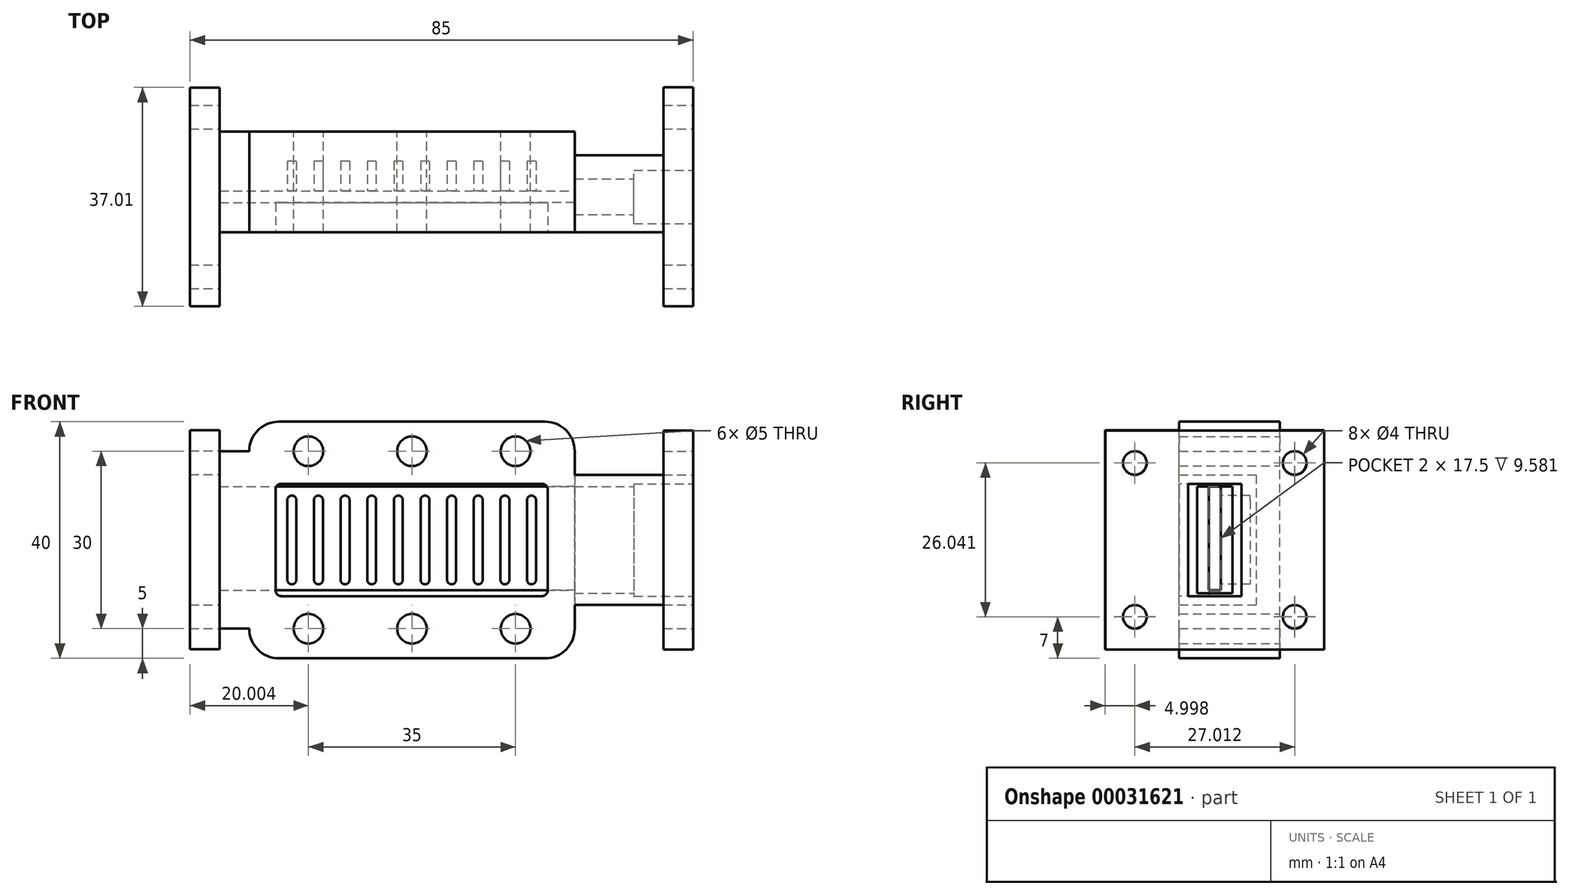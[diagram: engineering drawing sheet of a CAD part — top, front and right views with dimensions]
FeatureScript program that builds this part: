
annotation { "Feature Type Name" : "Feature", "Feature Type Description" : "" }
export const myFeature = defineFeature(function(context is Context, id is Id, definition is map)
    precondition{}
    {
        {
            var Q0;
            Q0=qCreatedBy(makeId("Front.planeOp"),FACE);
            var sketch = newSketch(context, id + "F0", { "sketchPlane" : qUnion([Q0])});
            skLineSegment(sketch, "E0.bottom", {"start": v(22.55, -20) * mm, "end": v(-22.45, -20) * mm});
            skLineSegment(sketch, "E0.top", {"start": v(22.55, 20) * mm, "end": v(-22.45, 20) * mm});
            skLineSegment(sketch, "E0.left", {"start": v(27.55, -15) * mm, "end": v(27.55, 15) * mm});
            skLineSegment(sketch, "E0.right", {"start": v(-27.45, -15) * mm, "end": v(-27.45, 15) * mm});
            skCircle(sketch, "E1", {"center": v(-17.45, 15) * mm, "radius": 2.5 * mm});
            skLineSegment(sketch, "E2", {"start": v(-40.3, 0) * mm, "end": v(38.37, 0) * mm, "construction": true});
            skCircle(sketch, "E3.MirrorC", {"center": v(-17.45, -15) * mm, "radius": 2.5 * mm});
            skCircle(sketch, "E4", {"center": v(0.05, 15) * mm, "radius": 2.5 * mm});
            skCircle(sketch, "E5", {"center": v(17.55, 15) * mm, "radius": 2.5 * mm});
            skCircle(sketch, "E6.MirrorC", {"center": v(0.05, -15) * mm, "radius": 2.5 * mm});
            skCircle(sketch, "E7.MirrorC", {"center": v(17.55, -15) * mm, "radius": 2.5 * mm});
            skPoint(sketch, "E8.visualSharp", {"position": v(-27.45, 20) * mm});
            skArc(sketch, "E8.filletArc", {"start": v(-22.45, 20) * mm, "mid": v(-25.98, 18.54) * mm, "end": v(-27.45, 15) * mm});
            skPoint(sketch, "E9.visualSharp", {"position": v(-27.45, -20) * mm});
            skArc(sketch, "E9.filletArc", {"start": v(-27.45, -15) * mm, "mid": v(-25.98, -18.54) * mm, "end": v(-22.45, -20) * mm});
            skPoint(sketch, "E10.visualSharp", {"position": v(27.55, -20) * mm});
            skArc(sketch, "E10.filletArc", {"start": v(22.55, -20) * mm, "mid": v(26.09, -18.54) * mm, "end": v(27.55, -15) * mm});
            skPoint(sketch, "E11.visualSharp", {"position": v(27.55, 20) * mm});
            skArc(sketch, "E11.filletArc", {"start": v(27.55, 15) * mm, "mid": v(26.09, 18.54) * mm, "end": v(22.55, 20) * mm});
            skSolve(sketch);
        }
        {
            var Q0;
            Q0=makeQuery(id+"F0.imprint","IMPRINT",FACE,{"disambiguationData":[TD([[makeQuery(id+"F0.imprint","IMPRINT",EDGE,{"derivedFrom":sQuery(id+"F0.wireOp",EDGE,"E0.bottom")}),-1.0]])]});
            extrude(context, id + "F1", {"entities" : qUnion([Q0]), "depth" : 17 * mm});
        }
        {
            var Q0;
            Q0=makeQuery(id+"F1.opExtrude","CAP_FACE",FACE,{"disambiguationData":[OSD([sQuery(id+"F0.wireOp",EDGE,"E0.bottom"),sQuery(id+"F0.wireOp",EDGE,"E0.top"),sQuery(id+"F0.wireOp",EDGE,"E0.left"),sQuery(id+"F0.wireOp",EDGE,"E0.right"),sQuery(id+"F0.wireOp",EDGE,"E1"),sQuery(id+"F0.wireOp",EDGE,"E3.MirrorC"),sQuery(id+"F0.wireOp",EDGE,"E4"),sQuery(id+"F0.wireOp",EDGE,"E5"),sQuery(id+"F0.wireOp",EDGE,"E6.MirrorC"),sQuery(id+"F0.wireOp",EDGE,"E7.MirrorC"),sQuery(id+"F0.wireOp",EDGE,"E8.filletArc"),sQuery(id+"F0.wireOp",EDGE,"E9.filletArc"),sQuery(id+"F0.wireOp",EDGE,"E10.filletArc"),sQuery(id+"F0.wireOp",EDGE,"E11.filletArc")])],"isStart":false});
            var sketch = newSketch(context, id + "F2", { "sketchPlane" : qUnion([Q0])});
            skLineSegment(sketch, "E12.bottom", {"start": v(-22, 9.5) * mm, "end": v(22, 9.5) * mm});
            skLineSegment(sketch, "E12.top", {"start": v(-22, -9.5) * mm, "end": v(22, -9.5) * mm});
            skLineSegment(sketch, "E12.left", {"start": v(-23, 8.5) * mm, "end": v(-23, -8.5) * mm});
            skLineSegment(sketch, "E12.right", {"start": v(23, 8.5) * mm, "end": v(23, -8.5) * mm});
            skLineSegment(sketch, "E13", {"start": v(-42.5, 0) * mm, "end": v(36.74, 0) * mm, "construction": true});
            skLineSegment(sketch, "E14", {"start": v(0, 24.37) * mm, "end": v(0, -28.4) * mm, "construction": true});
            skPoint(sketch, "E15.visualSharp", {"position": v(-23, 9.5) * mm});
            skArc(sketch, "E15.filletArc", {"start": v(-22, 9.5) * mm, "mid": v(-22.7, 9.2) * mm, "end": v(-23, 8.5) * mm});
            skPoint(sketch, "E16.visualSharp", {"position": v(-23, -9.5) * mm});
            skArc(sketch, "E16.filletArc", {"start": v(-23, -8.5) * mm, "mid": v(-22.7, -9.2) * mm, "end": v(-22, -9.5) * mm});
            skPoint(sketch, "E17.visualSharp", {"position": v(23, -9.5) * mm});
            skArc(sketch, "E17.filletArc", {"start": v(22, -9.5) * mm, "mid": v(22.7, -9.2) * mm, "end": v(23, -8.5) * mm});
            skPoint(sketch, "E18.visualSharp", {"position": v(23, 9.5) * mm});
            skArc(sketch, "E18.filletArc", {"start": v(23, 8.5) * mm, "mid": v(22.7, 9.2) * mm, "end": v(22, 9.5) * mm});
            skSolve(sketch);
        }
        {
            var Q0;
            Q0 = qSketchRegion(id + "F2", true);
            extrude(context, id + "F3", {"entities" : qUnion([Q0]), "operationType" : NewBodyOperationType.REMOVE, "oppositeDirection" : true, "depth" : 5 * mm});
        }
        {
            var Q0;
            Q0=makeQuery(id+"F3.boolean.opBoolean","COPY",FACE,{"derivedFrom":makeQuery(id+"F3.opExtrude","CAP_FACE",FACE,{"disambiguationData":[OSD([sQuery(id+"F2.wireOp",EDGE,"E12.bottom"),sQuery(id+"F2.wireOp",EDGE,"E12.top"),sQuery(id+"F2.wireOp",EDGE,"E12.left"),sQuery(id+"F2.wireOp",EDGE,"E12.right"),sQuery(id+"F2.wireOp",EDGE,"E15.filletArc"),sQuery(id+"F2.wireOp",EDGE,"E16.filletArc"),sQuery(id+"F2.wireOp",EDGE,"E17.filletArc"),sQuery(id+"F2.wireOp",EDGE,"E18.filletArc")])],"isStart":false})});
            var sketch = newSketch(context, id + "F4", { "sketchPlane" : qUnion([Q0])});
            skLineSegment(sketch, "E19.bottom", {"start": v(-23, 8.5) * mm, "end": v(23, 8.5) * mm});
            skLineSegment(sketch, "E19.top", {"start": v(-23, -8.5) * mm, "end": v(23, -8.5) * mm});
            skLineSegment(sketch, "E19.left", {"start": v(-23, 8.5) * mm, "end": v(-23, -8.5) * mm});
            skLineSegment(sketch, "E20", {"start": v(0, 22.62) * mm, "end": v(0, -29.48) * mm, "construction": true});
            skLineSegment(sketch, "E21", {"start": v(23, 8.5) * mm, "end": v(23, -8.5) * mm});
            skSolve(sketch);
        }
        {
            var Q0;
            Q0 = qSketchRegion(id + "F4", true);
            extrude(context, id + "F5", {"entities" : qUnion([Q0]), "operationType" : NewBodyOperationType.REMOVE, "oppositeDirection" : true, "depth" : 2 * mm});
        }
        {
            var Q0;
            Q0=makeQuery(id+"F5.boolean.opBoolean","COPY",FACE,{"derivedFrom":makeQuery(id+"F5.opExtrude","CAP_FACE",FACE,{"disambiguationData":[OSD([sQuery(id+"F4.wireOp",EDGE,"E19.bottom"),sQuery(id+"F4.wireOp",EDGE,"E19.top"),sQuery(id+"F4.wireOp",EDGE,"E19.left"),sQuery(id+"F4.wireOp",EDGE,"E21")])],"isStart":false})});
            var sketch = newSketch(context, id + "F6", { "sketchPlane" : qUnion([Q0])});
            skLineSegment(sketch, "E22.bottom", {"start": v(-20.25, 7.5) * mm, "end": v(-20.25, 7.5) * mm});
            skLineSegment(sketch, "E22.top", {"start": v(-20.25, -7.5) * mm, "end": v(-20.25, -7.5) * mm});
            skLineSegment(sketch, "E22.left", {"start": v(-21, 6.75) * mm, "end": v(-21, -6.75) * mm});
            skLineSegment(sketch, "E22.right", {"start": v(-19.5, 6.75) * mm, "end": v(-19.5, -6.75) * mm});
            skPoint(sketch, "E23.visualSharp", {"position": v(22.5, 9) * mm});
            skPoint(sketch, "E24.visualSharp", {"position": v(22.5, -9) * mm});
            skPoint(sketch, "E25.visualSharp", {"position": v(-22.5, -9) * mm});
            skPoint(sketch, "E26.visualSharp", {"position": v(-19.5, 7.5) * mm});
            skArc(sketch, "E26.filletArc", {"start": v(-19.5, 6.75) * mm, "mid": v(-19.72, 7.28) * mm, "end": v(-20.25, 7.5) * mm});
            skPoint(sketch, "E27.visualSharp", {"position": v(-21, 7.5) * mm});
            skArc(sketch, "E27.filletArc", {"start": v(-20.25, 7.5) * mm, "mid": v(-20.78, 7.28) * mm, "end": v(-21, 6.75) * mm});
            skPoint(sketch, "E28.visualSharp", {"position": v(-21, -7.5) * mm});
            skArc(sketch, "E28.filletArc", {"start": v(-21, -6.75) * mm, "mid": v(-20.78, -7.28) * mm, "end": v(-20.25, -7.5) * mm});
            skPoint(sketch, "E29.visualSharp", {"position": v(-19.5, -7.5) * mm});
            skArc(sketch, "E29.filletArc", {"start": v(-20.25, -7.5) * mm, "mid": v(-19.72, -7.28) * mm, "end": v(-19.5, -6.75) * mm});
            skLineSegment(sketch, "E30.1.0.0", {"start": v(-16.5, 6.75) * mm, "end": v(-16.5, -6.75) * mm});
            skArc(sketch, "E30.1.0.1", {"start": v(-15.75, 7.5) * mm, "mid": v(-16.28, 7.28) * mm, "end": v(-16.5, 6.75) * mm});
            skArc(sketch, "E30.1.0.2", {"start": v(-15, 6.75) * mm, "mid": v(-15.22, 7.28) * mm, "end": v(-15.75, 7.5) * mm});
            skLineSegment(sketch, "E30.1.0.3", {"start": v(-15, 6.75) * mm, "end": v(-15, -6.75) * mm});
            skArc(sketch, "E30.1.0.4", {"start": v(-15.75, -7.5) * mm, "mid": v(-15.22, -7.28) * mm, "end": v(-15, -6.75) * mm});
            skArc(sketch, "E30.1.0.5", {"start": v(-16.5, -6.75) * mm, "mid": v(-16.28, -7.28) * mm, "end": v(-15.75, -7.5) * mm});
            skLineSegment(sketch, "E30.2.0.0", {"start": v(-12, 6.75) * mm, "end": v(-12, -6.75) * mm});
            skArc(sketch, "E30.2.0.1", {"start": v(-11.25, 7.5) * mm, "mid": v(-11.78, 7.28) * mm, "end": v(-12, 6.75) * mm});
            skArc(sketch, "E30.2.0.2", {"start": v(-10.5, 6.75) * mm, "mid": v(-10.72, 7.28) * mm, "end": v(-11.25, 7.5) * mm});
            skLineSegment(sketch, "E30.2.0.3", {"start": v(-10.5, 6.75) * mm, "end": v(-10.5, -6.75) * mm});
            skArc(sketch, "E30.2.0.4", {"start": v(-11.25, -7.5) * mm, "mid": v(-10.72, -7.28) * mm, "end": v(-10.5, -6.75) * mm});
            skArc(sketch, "E30.2.0.5", {"start": v(-12, -6.75) * mm, "mid": v(-11.78, -7.28) * mm, "end": v(-11.25, -7.5) * mm});
            skLineSegment(sketch, "E30.direction1", {"start": v(-21, -6.75) * mm, "end": v(-16.5, -6.75) * mm, "construction": true});
            skLineSegment(sketch, "E31.0.3.0", {"start": v(-7.5, 6.75) * mm, "end": v(-7.5, -6.75) * mm});
            skArc(sketch, "E31.3.3.0", {"start": v(-6.75, 7.5) * mm, "mid": v(-7.28, 7.28) * mm, "end": v(-7.5, 6.75) * mm});
            skArc(sketch, "E31.7.3.0", {"start": v(-6, 6.75) * mm, "mid": v(-6.22, 7.28) * mm, "end": v(-6.75, 7.5) * mm});
            skLineSegment(sketch, "E31.11.3.0", {"start": v(-6, 6.75) * mm, "end": v(-6, -6.75) * mm});
            skArc(sketch, "E31.14.3.0", {"start": v(-6.75, -7.5) * mm, "mid": v(-6.22, -7.28) * mm, "end": v(-6, -6.75) * mm});
            skArc(sketch, "E31.18.3.0", {"start": v(-7.5, -6.75) * mm, "mid": v(-7.28, -7.28) * mm, "end": v(-6.75, -7.5) * mm});
            skLineSegment(sketch, "E31.0.4.0", {"start": v(-3, 6.75) * mm, "end": v(-3, -6.75) * mm});
            skArc(sketch, "E31.3.4.0", {"start": v(-2.25, 7.5) * mm, "mid": v(-2.78, 7.28) * mm, "end": v(-3, 6.75) * mm});
            skArc(sketch, "E31.7.4.0", {"start": v(-1.5, 6.75) * mm, "mid": v(-1.72, 7.28) * mm, "end": v(-2.25, 7.5) * mm});
            skLineSegment(sketch, "E31.11.4.0", {"start": v(-1.5, 6.75) * mm, "end": v(-1.5, -6.75) * mm});
            skArc(sketch, "E31.14.4.0", {"start": v(-2.25, -7.5) * mm, "mid": v(-1.72, -7.28) * mm, "end": v(-1.5, -6.75) * mm});
            skArc(sketch, "E31.18.4.0", {"start": v(-3, -6.75) * mm, "mid": v(-2.78, -7.28) * mm, "end": v(-2.25, -7.5) * mm});
            skLineSegment(sketch, "E31.0.5.0", {"start": v(1.5, 6.75) * mm, "end": v(1.5, -6.75) * mm});
            skArc(sketch, "E31.3.5.0", {"start": v(2.25, 7.5) * mm, "mid": v(1.72, 7.28) * mm, "end": v(1.5, 6.75) * mm});
            skArc(sketch, "E31.7.5.0", {"start": v(3, 6.75) * mm, "mid": v(2.78, 7.28) * mm, "end": v(2.25, 7.5) * mm});
            skLineSegment(sketch, "E31.11.5.0", {"start": v(3, 6.75) * mm, "end": v(3, -6.75) * mm});
            skArc(sketch, "E31.14.5.0", {"start": v(2.25, -7.5) * mm, "mid": v(2.78, -7.28) * mm, "end": v(3, -6.75) * mm});
            skArc(sketch, "E31.18.5.0", {"start": v(1.5, -6.75) * mm, "mid": v(1.72, -7.28) * mm, "end": v(2.25, -7.5) * mm});
            skLineSegment(sketch, "E31.0.6.0", {"start": v(6, 6.75) * mm, "end": v(6, -6.75) * mm});
            skArc(sketch, "E31.3.6.0", {"start": v(6.75, 7.5) * mm, "mid": v(6.22, 7.28) * mm, "end": v(6, 6.75) * mm});
            skArc(sketch, "E31.7.6.0", {"start": v(7.5, 6.75) * mm, "mid": v(7.28, 7.28) * mm, "end": v(6.75, 7.5) * mm});
            skLineSegment(sketch, "E31.11.6.0", {"start": v(7.5, 6.75) * mm, "end": v(7.5, -6.75) * mm});
            skArc(sketch, "E31.14.6.0", {"start": v(6.75, -7.5) * mm, "mid": v(7.28, -7.28) * mm, "end": v(7.5, -6.75) * mm});
            skArc(sketch, "E31.18.6.0", {"start": v(6, -6.75) * mm, "mid": v(6.22, -7.28) * mm, "end": v(6.75, -7.5) * mm});
            skLineSegment(sketch, "E31.0.7.0", {"start": v(10.5, 6.75) * mm, "end": v(10.5, -6.75) * mm});
            skArc(sketch, "E31.3.7.0", {"start": v(11.25, 7.5) * mm, "mid": v(10.72, 7.28) * mm, "end": v(10.5, 6.75) * mm});
            skArc(sketch, "E31.7.7.0", {"start": v(12, 6.75) * mm, "mid": v(11.78, 7.28) * mm, "end": v(11.25, 7.5) * mm});
            skLineSegment(sketch, "E31.11.7.0", {"start": v(12, 6.75) * mm, "end": v(12, -6.75) * mm});
            skArc(sketch, "E31.14.7.0", {"start": v(11.25, -7.5) * mm, "mid": v(11.78, -7.28) * mm, "end": v(12, -6.75) * mm});
            skArc(sketch, "E31.18.7.0", {"start": v(10.5, -6.75) * mm, "mid": v(10.72, -7.28) * mm, "end": v(11.25, -7.5) * mm});
            skLineSegment(sketch, "E31.0.8.0", {"start": v(15, 6.75) * mm, "end": v(15, -6.75) * mm});
            skArc(sketch, "E31.3.8.0", {"start": v(15.75, 7.5) * mm, "mid": v(15.22, 7.28) * mm, "end": v(15, 6.75) * mm});
            skArc(sketch, "E31.7.8.0", {"start": v(16.5, 6.75) * mm, "mid": v(16.28, 7.28) * mm, "end": v(15.75, 7.5) * mm});
            skLineSegment(sketch, "E31.11.8.0", {"start": v(16.5, 6.75) * mm, "end": v(16.5, -6.75) * mm});
            skArc(sketch, "E31.14.8.0", {"start": v(15.75, -7.5) * mm, "mid": v(16.28, -7.28) * mm, "end": v(16.5, -6.75) * mm});
            skArc(sketch, "E31.18.8.0", {"start": v(15, -6.75) * mm, "mid": v(15.22, -7.28) * mm, "end": v(15.75, -7.5) * mm});
            skLineSegment(sketch, "E31.0.9.0", {"start": v(19.5, 6.75) * mm, "end": v(19.5, -6.75) * mm});
            skArc(sketch, "E31.3.9.0", {"start": v(20.25, 7.5) * mm, "mid": v(19.72, 7.28) * mm, "end": v(19.5, 6.75) * mm});
            skArc(sketch, "E31.7.9.0", {"start": v(21, 6.75) * mm, "mid": v(20.78, 7.28) * mm, "end": v(20.25, 7.5) * mm});
            skLineSegment(sketch, "E31.11.9.0", {"start": v(21, 6.75) * mm, "end": v(21, -6.75) * mm});
            skArc(sketch, "E31.14.9.0", {"start": v(20.25, -7.5) * mm, "mid": v(20.78, -7.28) * mm, "end": v(21, -6.75) * mm});
            skArc(sketch, "E31.18.9.0", {"start": v(19.5, -6.75) * mm, "mid": v(19.72, -7.28) * mm, "end": v(20.25, -7.5) * mm});
            skSolve(sketch);
        }
        {
            var Q0;
            Q0 = qSketchRegion(id + "F6", true);
            extrude(context, id + "F7", {"entities" : qUnion([Q0]), "operationType" : NewBodyOperationType.REMOVE, "oppositeDirection" : true, "depth" : 5 * mm});
        }
        {
            var Q0;
            Q0=makeQuery(id+"F1.opExtrude","SWEPT_FACE",FACE,{"disambiguationData":[OSD([sQuery(id+"F0.wireOp",EDGE,"E0.right")])]});
            var sketch = newSketch(context, id + "F8", { "sketchPlane" : qUnion([Q0])});
            skLineSegment(sketch, "E32.bottom", {"start": v(10, 9) * mm, "end": v(12, 9) * mm});
            skLineSegment(sketch, "E32.top", {"start": v(10, -8.5) * mm, "end": v(12, -8.5) * mm});
            skLineSegment(sketch, "E32.left", {"start": v(10, 9) * mm, "end": v(10, -8.5) * mm});
            skLineSegment(sketch, "E32.right", {"start": v(12, 9) * mm, "end": v(12, -8.5) * mm});
            skLineSegment(sketch, "E33", {"start": v(23.3, 0) * mm, "end": v(0, 0) * mm, "construction": true});
            skSolve(sketch);
        }
        {
            var Q0;
            Q0=makeQuery(id+"F1.opExtrude","SWEPT_FACE",FACE,{"disambiguationData":[OSD([sQuery(id+"F0.wireOp",EDGE,"E0.left")])]});
            var sketch = newSketch(context, id + "F9", { "sketchPlane" : qUnion([Q0])});
            skLineSegment(sketch, "E34.bottom", {"start": v(-17, 11) * mm, "end": v(-4, 11) * mm});
            skLineSegment(sketch, "E34.top", {"start": v(-17, -11) * mm, "end": v(-4, -11) * mm});
            skLineSegment(sketch, "E34.left", {"start": v(-17, 11) * mm, "end": v(-17, -11) * mm});
            skLineSegment(sketch, "E34.right", {"start": v(-4, 11) * mm, "end": v(-4, -11) * mm});
            skLineSegment(sketch, "E35", {"start": v(-20.32, 0) * mm, "end": v(5.52, 0) * mm, "construction": true});
            skLineSegment(sketch, "E36", {"start": v(0, 0) * mm, "end": v(0, 23.79) * mm, "construction": true});
            skSolve(sketch);
        }
        {
            var Q0;
            Q0 = qSketchRegion(id + "F9", true);
            extrude(context, id + "F10", {"entities" : qUnion([Q0]), "operationType" : NewBodyOperationType.ADD, "depth" : 20 * mm});
        }
        {
            var Q0;
            Q0=makeQuery(id+"F10.opExtrude","CAP_FACE",FACE,{"disambiguationData":[OSD([sQuery(id+"F9.wireOp",EDGE,"E34.bottom"),sQuery(id+"F9.wireOp",EDGE,"E34.top"),sQuery(id+"F9.wireOp",EDGE,"E34.left"),sQuery(id+"F9.wireOp",EDGE,"E34.right")])],"isStart":false});
            var sketch = newSketch(context, id + "F11", { "sketchPlane" : qUnion([Q0])});
            skLineSegment(sketch, "E37.bottom", {"start": v(-29.5, 18.5) * mm, "end": v(7.5, 18.5) * mm});
            skLineSegment(sketch, "E37.top", {"start": v(-29.5, -18.5) * mm, "end": v(7.5, -18.5) * mm});
            skLineSegment(sketch, "E37.left", {"start": v(-29.5, 18.5) * mm, "end": v(-29.5, -18.5) * mm});
            skLineSegment(sketch, "E37.right", {"start": v(7.5, 18.5) * mm, "end": v(7.5, -18.5) * mm});
            skCircle(sketch, "E38", {"center": v(-24.5, -13) * mm, "radius": 2 * mm});
            skCircle(sketch, "E39", {"center": v(2.5, -13) * mm, "radius": 2 * mm});
            skLineSegment(sketch, "E40", {"start": v(-37.5, 0) * mm, "end": v(67.03, 0) * mm, "construction": true});
            skCircle(sketch, "E41.MirrorC", {"center": v(2.5, 13) * mm, "radius": 2 * mm});
            skCircle(sketch, "E42.MirrorC", {"center": v(-24.5, 13) * mm, "radius": 2 * mm});
            skSolve(sketch);
        }
        {
            var Q0;
            Q0=makeQuery(id+"F11.imprint","IMPRINT",FACE,{"disambiguationData":[TD([[makeQuery(id+"F11.imprint","IMPRINT",EDGE,{"derivedFrom":sQuery(id+"F11.wireOp",EDGE,"E37.bottom")}),-1.0]])]});
            extrude(context, id + "F12", {"entities" : qUnion([Q0]), "operationType" : NewBodyOperationType.ADD, "oppositeDirection" : true, "depth" : 5 * mm});
        }
        {
            var Q0;
            {var subQ0=sQuery(id+"F9.wireOp",EDGE,"E34.bottom");var subQ1=sQuery(id+"F9.wireOp",EDGE,"E34.top");var subQ2=sQuery(id+"F9.wireOp",EDGE,"E34.left");var subQ3=sQuery(id+"F9.wireOp",EDGE,"E34.right");Q0=makeQuery(id+"F12.boolean.opBoolean","MERGE",FACE,{"derivedFrom":[makeQuery(id+"F10.opExtrude","CAP_FACE",FACE,{"disambiguationData":[OSD([subQ0,subQ1,subQ2,subQ3])],"isStart":false}),makeQuery(id+"F12.opExtrude","CAP_FACE",FACE,{"disambiguationData":[OSD([subQ0,subQ1,subQ2,subQ3,sQuery(id+"F11.wireOp",EDGE,"E37.bottom"),sQuery(id+"F11.wireOp",EDGE,"E37.top"),sQuery(id+"F11.wireOp",EDGE,"E37.left"),sQuery(id+"F11.wireOp",EDGE,"E37.right"),sQuery(id+"F11.wireOp",EDGE,"E38"),sQuery(id+"F11.wireOp",EDGE,"E39"),sQuery(id+"F11.wireOp",EDGE,"E41.MirrorC"),sQuery(id+"F11.wireOp",EDGE,"E42.MirrorC")])],"isStart":true})]});}
            var sketch = newSketch(context, id + "F13", { "sketchPlane" : qUnion([Q0])});
            skLineSegment(sketch, "E43.bottom", {"start": v(-15.5, 9.5) * mm, "end": v(-6.5, 9.5) * mm});
            skLineSegment(sketch, "E43.top", {"start": v(-15.5, -9.5) * mm, "end": v(-6.5, -9.5) * mm});
            skLineSegment(sketch, "E43.left", {"start": v(-15.5, 9.5) * mm, "end": v(-15.5, -9.5) * mm});
            skLineSegment(sketch, "E43.right", {"start": v(-6.5, 9.5) * mm, "end": v(-6.5, -9.5) * mm});
            skLineSegment(sketch, "E44", {"start": v(-24.98, 0) * mm, "end": v(12.3, 0) * mm, "construction": true});
            skSolve(sketch);
        }
        {
            var Q0;
            Q0=makeQuery(id+"F13.imprint","IMPRINT",FACE,{"disambiguationData":[TD([[makeQuery(id+"F13.imprint","IMPRINT",EDGE,{"derivedFrom":sQuery(id+"F13.wireOp",EDGE,"E43.bottom")}),-1.0]])]});
            extrude(context, id + "F14", {"entities" : qUnion([Q0]), "operationType" : NewBodyOperationType.REMOVE, "oppositeDirection" : true, "depth" : 10 * mm});
        }
        {
            var Q0;
            Q0=makeQuery(id+"F14.boolean.opBoolean","COPY",FACE,{"derivedFrom":makeQuery(id+"F14.opExtrude","CAP_FACE",FACE,{"disambiguationData":[OSD([sQuery(id+"F13.wireOp",EDGE,"E43.bottom"),sQuery(id+"F13.wireOp",EDGE,"E43.top"),sQuery(id+"F13.wireOp",EDGE,"E43.left"),sQuery(id+"F13.wireOp",EDGE,"E43.right")])],"isStart":false})});
            var sketch = newSketch(context, id + "F15", { "sketchPlane" : qUnion([Q0])});
            skLineSegment(sketch, "E45.bottom", {"start": v(-14, 9) * mm, "end": v(-8, 9) * mm});
            skLineSegment(sketch, "E45.top", {"start": v(-14, -9) * mm, "end": v(-8, -9) * mm});
            skLineSegment(sketch, "E45.left", {"start": v(-14, 9) * mm, "end": v(-14, -9) * mm});
            skLineSegment(sketch, "E45.right", {"start": v(-8, 9) * mm, "end": v(-8, -9) * mm});
            skSolve(sketch);
        }
        {
            var Q0;
            Q0=makeQuery(id+"F15.imprint","IMPRINT",FACE,{"disambiguationData":[TD([[makeQuery(id+"F15.imprint","IMPRINT",EDGE,{"derivedFrom":sQuery(id+"F15.wireOp",EDGE,"E45.bottom")}),-1.0]])]});
            extrude(context, id + "F16", {"entities" : qUnion([Q0]), "operationType" : NewBodyOperationType.REMOVE, "oppositeDirection" : true, "depth" : 10 * mm});
        }
        {
            var Q0;
            Q0=makeQuery(id+"F8.imprint","IMPRINT",FACE,{"disambiguationData":[TD([[makeQuery(id+"F8.imprint","IMPRINT",EDGE,{"derivedFrom":sQuery(id+"F8.wireOp",EDGE,"E32.bottom")}),1.0]])]});
            extrude(context, id + "F17", {"entities" : qUnion([Q0]), "operationType" : NewBodyOperationType.ADD, "depth" : 5 * mm});
        }
        {
            var Q0;
            Q0=makeQuery(id+"F17.opExtrude","CAP_FACE",FACE,{"disambiguationData":[OSD([sQuery(id+"F0.wireOp",EDGE,"E0.right"),sQuery(id+"F0.wireOp",EDGE,"E8.filletArc"),sQuery(id+"F0.wireOp",EDGE,"E9.filletArc"),sQuery(id+"F8.wireOp",EDGE,"E32.bottom"),sQuery(id+"F8.wireOp",EDGE,"E32.top"),sQuery(id+"F8.wireOp",EDGE,"E32.left"),sQuery(id+"F8.wireOp",EDGE,"E32.right")])],"isStart":false});
            var sketch = newSketch(context, id + "F18", { "sketchPlane" : qUnion([Q0])});
            skLineSegment(sketch, "E46.bottom", {"start": v(-7.49, 18.54) * mm, "end": v(29.51, 18.54) * mm});
            skLineSegment(sketch, "E46.top", {"start": v(-7.49, -18.46) * mm, "end": v(29.51, -18.46) * mm});
            skLineSegment(sketch, "E46.left", {"start": v(-7.49, 18.54) * mm, "end": v(-7.49, -18.46) * mm});
            skLineSegment(sketch, "E46.right", {"start": v(29.51, 18.54) * mm, "end": v(29.51, -18.46) * mm});
            skCircle(sketch, "E47", {"center": v(-2.49, -12.96) * mm, "radius": 2 * mm});
            skCircle(sketch, "E48", {"center": v(24.51, -12.96) * mm, "radius": 2 * mm});
            skLineSegment(sketch, "E49", {"start": v(-15.5, 0.04) * mm, "end": v(89.05, 0.04) * mm, "construction": true});
            skCircle(sketch, "E50.MirrorC", {"center": v(24.51, 13.04) * mm, "radius": 2 * mm});
            skCircle(sketch, "E51.MirrorC", {"center": v(-2.49, 13.04) * mm, "radius": 2 * mm});
            skSolve(sketch);
        }
        {
            var Q0;
            Q0 = qSketchRegion(id + "F18", true);
            var Q1;
            Q1 = qConstructionFilter(qBodyType(qCreatedBy(id + "F18" ,EDGE), BodyType.WIRE), ConstructionObject.NO);
            extrude(context, id + "F19", {"entities" : qUnion([Q0]), "operationType" : NewBodyOperationType.ADD, "surfaceEntities" : qUnion([Q1]), "depth" : 5 * mm});
        }
        {
            var Q0;
            Q0 = qSketchRegion(id + "F8", true);
            extrude(context, id + "F20", {"entities" : qUnion([Q0]), "operationType" : NewBodyOperationType.REMOVE, "endBound" : BoundingType.THROUGH_ALL, "oppositeDirection" : true, "depth" : 60 * mm});
        }
    });
